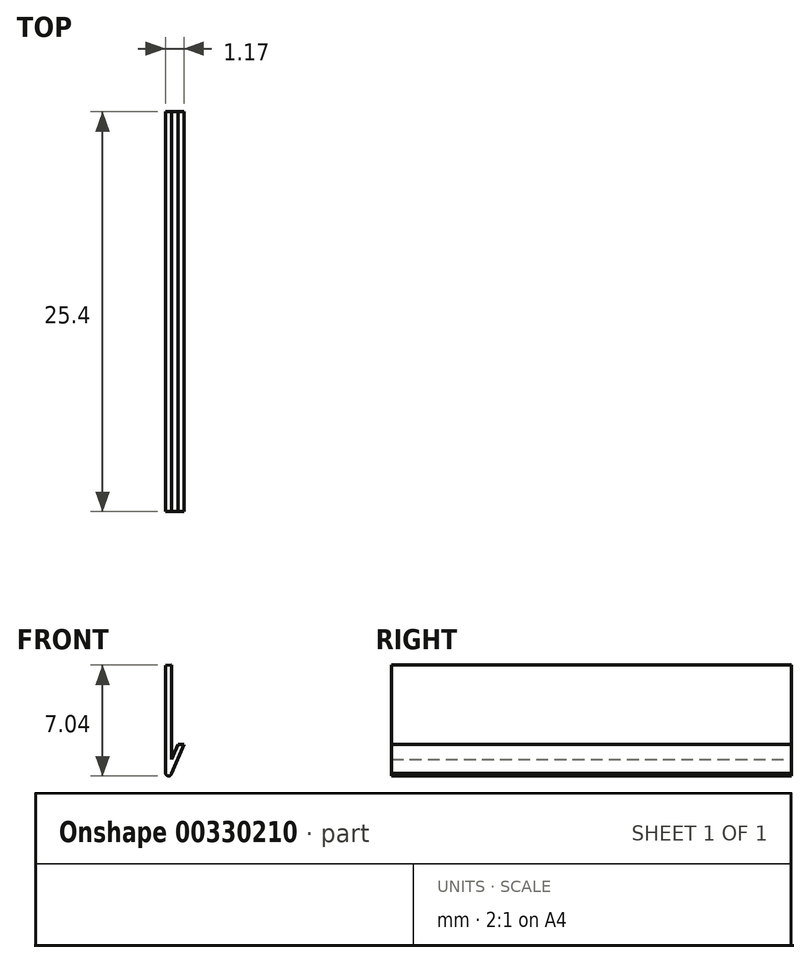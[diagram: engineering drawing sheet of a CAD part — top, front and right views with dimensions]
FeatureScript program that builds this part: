
annotation { "Feature Type Name" : "Feature", "Feature Type Description" : "" }
export const myFeature = defineFeature(function(context is Context, id is Id, definition is map)
    precondition{}
    {
        {
            var Q0;
            Q0=qCreatedBy(makeId("Front.planeOp"),FACE);
            var sketch = newSketch(context, id + "F0", { "sketchPlane" : qUnion([Q0])});
            skLineSegment(sketch, "E0", {"start": v(0, 6) * mm, "end": v(0, 0) * mm});
            skLineSegment(sketch, "E1", {"start": v(-0.4, 5.98) * mm, "end": v(-0.4, -0.86) * mm});
            skLineSegment(sketch, "E2", {"start": v(-0.4, 5.98) * mm, "end": v(0, 6) * mm});
            skArc(sketch, "E3", {"start": v(-0.4, -0.86) * mm, "mid": v(-0.2, -1.05) * mm, "end": v(0, -0.88) * mm});
            skLineSegment(sketch, "E4", {"start": v(0, -0.88) * mm, "end": v(0.78, 0.96) * mm});
            skLineSegment(sketch, "E5", {"start": v(0.78, 0.96) * mm, "end": v(0.42, 0.96) * mm});
            skLineSegment(sketch, "E6", {"start": v(0.42, 0.96) * mm, "end": v(0, 0) * mm});
            skSolve(sketch);
        }
        {
            var Q0;
            Q0=makeQuery(id+"F0.imprint","IMPRINT",FACE,{"disambiguationData":[TD([[makeQuery(id+"F0.imprint","IMPRINT",EDGE,{"derivedFrom":sQuery(id+"F0.wireOp",EDGE,"E0")}),-1.0]])]});
            extrude(context, id + "F1", {"entities" : qUnion([Q0]), "depth" : 25.4 * mm});
        }
    });
